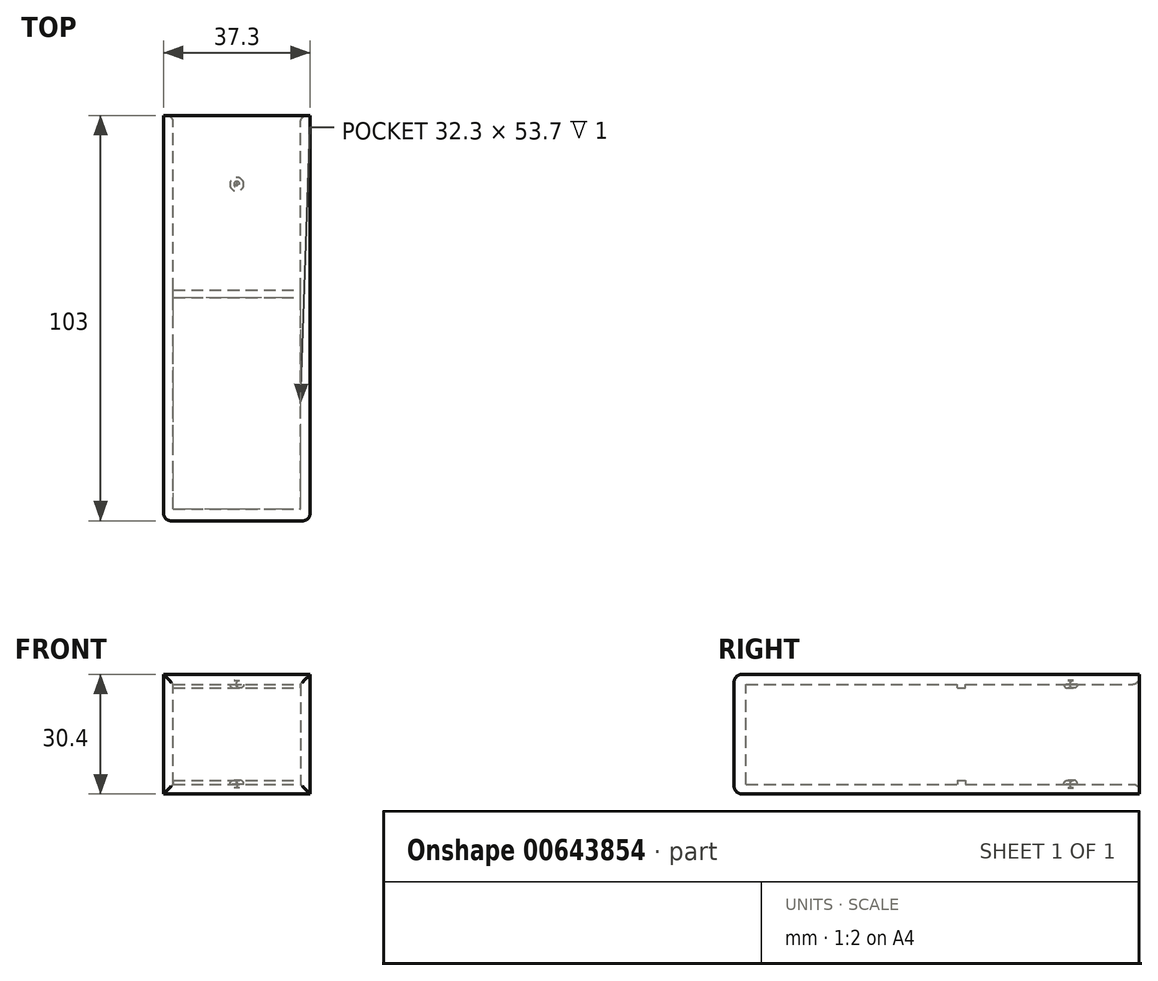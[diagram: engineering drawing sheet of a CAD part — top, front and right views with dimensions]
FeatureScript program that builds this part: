
annotation { "Feature Type Name" : "Feature", "Feature Type Description" : "" }
export const myFeature = defineFeature(function(context is Context, id is Id, definition is map)
    precondition{}
    {
        {
            var Q0;
            Q0=qCreatedBy(makeId("Front.planeOp"),FACE);
            var sketch = newSketch(context, id + "F0", { "sketchPlane" : qUnion([Q0])});
            skLineSegment(sketch, "E0.top", {"start": v(-16.49, 15.07) * mm, "end": v(15.81, 15.07) * mm});
            skLineSegment(sketch, "E0.left", {"start": v(-16.49, -10.33) * mm, "end": v(-16.49, 15.07) * mm});
            skLineSegment(sketch, "E1", {"start": v(15.81, 15.07) * mm, "end": v(15.81, -10.33) * mm});
            skLineSegment(sketch, "E2", {"start": v(-16.49, -10.33) * mm, "end": v(15.81, -10.33) * mm});
            skLineSegment(sketch, "E3.0", {"start": v(-18.99, 17.57) * mm, "end": v(18.31, 17.57) * mm});
            skLineSegment(sketch, "E3.1", {"start": v(-18.99, -12.83) * mm, "end": v(-18.99, 17.57) * mm});
            skLineSegment(sketch, "E3.2", {"start": v(-18.99, -12.83) * mm, "end": v(18.31, -12.83) * mm});
            skLineSegment(sketch, "E3.3", {"start": v(18.31, 17.57) * mm, "end": v(18.31, -12.83) * mm});
            skSolve(sketch);
        }
        {
            var Q0;
            Q0 = qSketchRegion(id + "F0", true);
            extrude(context, id + "F1", {"entities" : qUnion([Q0]), "depth" : 100 * mm, "offsetDistance" : 25 * mm});
        }
        {
            var Q0;
            Q0=makeQuery(id+"F1.opExtrude","CAP_FACE",FACE,{"disambiguationData":[OSD([sQuery(id+"F0.wireOp",EDGE,"E0.top"),sQuery(id+"F0.wireOp",EDGE,"E0.left"),sQuery(id+"F0.wireOp",EDGE,"E1"),sQuery(id+"F0.wireOp",EDGE,"E2"),sQuery(id+"F0.wireOp",EDGE,"E3.0"),sQuery(id+"F0.wireOp",EDGE,"E3.1"),sQuery(id+"F0.wireOp",EDGE,"E3.2"),sQuery(id+"F0.wireOp",EDGE,"E3.3")])],"isStart":false});
            var sketch = newSketch(context, id + "F2", { "sketchPlane" : qUnion([Q0])});
            skLineSegment(sketch, "E4.bottom", {"start": v(-18.99, 17.57) * mm, "end": v(18.31, 17.57) * mm});
            skLineSegment(sketch, "E4.top", {"start": v(-18.99, -12.83) * mm, "end": v(18.31, -12.83) * mm});
            skLineSegment(sketch, "E4.left", {"start": v(-18.99, 17.57) * mm, "end": v(-18.99, -12.83) * mm});
            skLineSegment(sketch, "E4.right", {"start": v(18.31, 17.57) * mm, "end": v(18.31, -12.83) * mm});
            skSolve(sketch);
        }
        {
            var Q0;
            Q0 = qSketchRegion(id + "F2", true);
            extrude(context, id + "F3", {"entities" : qUnion([Q0]), "operationType" : NewBodyOperationType.ADD, "depth" : 3 * mm, "offsetDistance" : 25 * mm});
        }
        {
            var Q0;
            Q0=makeQuery(id+"F3.opExtrude","CAP_FACE",FACE,{"disambiguationData":[OSD([sQuery(id+"F2.wireOp",EDGE,"E4.bottom"),sQuery(id+"F2.wireOp",EDGE,"E4.top"),sQuery(id+"F2.wireOp",EDGE,"E4.left"),sQuery(id+"F2.wireOp",EDGE,"E4.right")])],"isStart":false});
            fillet(context, id + "F4", {"entities" : qUnion([Q0]), "radius" : 2 * mm, "tangentPropagation" : true, "allowEdgeOverflow" : false});
        }
        {
            var Q0;
            Q0=makeQuery(id+"F1.opExtrude","CAP_EDGE",EDGE,{"disambiguationData":[OSD([sQuery(id+"F0.wireOp",EDGE,"E1")])],"isStart":true});
            var Q1;
            Q1=makeQuery(id+"F1.opExtrude","CAP_EDGE",EDGE,{"disambiguationData":[OSD([sQuery(id+"F0.wireOp",EDGE,"E0.top")])],"isStart":true});
            var Q2;
            Q2=makeQuery(id+"F1.opExtrude","CAP_EDGE",EDGE,{"disambiguationData":[OSD([sQuery(id+"F0.wireOp",EDGE,"E0.left")])],"isStart":true});
            var Q3;
            Q3=makeQuery(id+"F1.opExtrude","CAP_EDGE",EDGE,{"disambiguationData":[OSD([sQuery(id+"F0.wireOp",EDGE,"E2")])],"isStart":true});
            fillet(context, id + "F5", {"entities" : qUnion([Q0, Q1, Q2, Q3]), "radius" : 1.75 * mm, "tangentPropagation" : true, "allowEdgeOverflow" : false});
        }
        {
            var Q0;
            Q0=makeQuery(id+"F1.opExtrude","SWEPT_FACE",FACE,{"disambiguationData":[OSD([sQuery(id+"F0.wireOp",EDGE,"E2")])]});
            var sketch = newSketch(context, id + "F6", { "sketchPlane" : qUnion([Q0])});
            skPoint(sketch, "E5.0", {"position": v(-0.34, -1.75) * mm});
            skLineSegment(sketch, "E6", {"start": v(-0.34, -1.75) * mm, "end": v(-0.34, -20.52) * mm, "construction": true});
            skCircle(sketch, "E7", {"center": v(-0.34, -17.5) * mm, "radius": 1.75 * mm});
            skLineSegment(sketch, "E8.0", {"start": v(-18.24, 0) * mm, "end": v(17.56, 0) * mm});
            skSolve(sketch);
        }
        {
            var Q0;
            Q0 = qSketchRegion(id + "F6", true);
            extrude(context, id + "F7", {"entities" : qUnion([Q0]), "operationType" : NewBodyOperationType.REMOVE, "oppositeDirection" : true, "depth" : 1 * mm, "offsetDistance" : 25 * mm});
        }
        {
            var Q0;
            Q0=makeQuery(id+"F7.boolean.opBoolean","COPY",FACE,{"derivedFrom":makeQuery(id+"F7.opExtrude","CAP_FACE",FACE,{"disambiguationData":[OSD([sQuery(id+"F6.wireOp",EDGE,"E7")])],"isStart":false})});
            fillet(context, id + "F8", {"entities" : qUnion([Q0]), "radius" : 1 * mm, "tangentPropagation" : true, "allowEdgeOverflow" : false});
        }
        {
            var Q0;
            Q0=makeQuery(id+"F1.opExtrude","SWEPT_FACE",FACE,{"disambiguationData":[OSD([sQuery(id+"F0.wireOp",EDGE,"E0.top")])]});
            var sketch = newSketch(context, id + "F9", { "sketchPlane" : qUnion([Q0])});
            skCircle(sketch, "E9.0", {"center": v(-0.34, 17.5) * mm, "radius": 1.75 * mm});
            skSolve(sketch);
        }
        {
            var Q0;
            Q0 = qSketchRegion(id + "F9", true);
            extrude(context, id + "F10", {"entities" : qUnion([Q0]), "operationType" : NewBodyOperationType.REMOVE, "oppositeDirection" : true, "depth" : 1 * mm, "offsetDistance" : 25 * mm});
        }
        {
            var Q0;
            Q0=makeQuery(id+"F10.boolean.opBoolean","COPY",EDGE,{"derivedFrom":makeQuery(id+"F10.opExtrude","CAP_EDGE",EDGE,{"disambiguationData":[OSD([sQuery(id+"F9.wireOp",EDGE,"E9.0")])],"isStart":false})});
            fillet(context, id + "F11", {"entities" : qUnion([Q0]), "radius" : 1 * mm, "tangentPropagation" : true, "allowEdgeOverflow" : false});
        }
        {
            var Q0;
            Q0=makeQuery(id+"F1.opExtrude","SWEPT_FACE",FACE,{"disambiguationData":[OSD([sQuery(id+"F0.wireOp",EDGE,"E2")])]});
            var sketch = newSketch(context, id + "F12", { "sketchPlane" : qUnion([Q0])});
            skLineSegment(sketch, "E10", {"start": v(-16.49, -44.3) * mm, "end": v(15.81, -44.3) * mm});
            skCircle(sketch, "E11.0", {"center": v(-0.34, -17.5) * mm, "radius": 0.75 * mm, "construction": true});
            skCircle(sketch, "E12.0.0", {"center": v(-0.34, -17.5) * mm, "radius": 0.75 * mm});
            skLineSegment(sketch, "E13.0", {"start": v(-16.49, -46.3) * mm, "end": v(15.81, -46.3) * mm});
            skLineSegment(sketch, "E14.0", {"start": v(-29.33, 10.35) * mm, "end": v(-29.33, -111.35) * mm});
            skLineSegment(sketch, "E14.1", {"start": v(28.66, 10.35) * mm, "end": v(-29.33, 10.35) * mm});
            skLineSegment(sketch, "E14.2", {"start": v(28.66, -111.35) * mm, "end": v(28.66, 10.35) * mm});
            skLineSegment(sketch, "E14.3", {"start": v(-29.33, -111.35) * mm, "end": v(28.66, -111.35) * mm});
            skSolve(sketch);
        }
        {
            var Q0;
            {var subQ0=sQuery(id+"F12.wireOp",EDGE,"E10");Q0=makeQuery(id+"F12.imprint","IMPRINT",FACE,{"disambiguationData":[TD([[makeQuery(id+"F12.imprint","IMPRINT",EDGE,{"derivedFrom":subQ0}),-1.0]])]});}
            extrude(context, id + "F13", {"entities" : qUnion([Q0]), "operationType" : NewBodyOperationType.ADD, "depth" : 1 * mm, "offsetDistance" : 25 * mm});
        }
        {
            var Q0;
            Q0=makeQuery(id+"F1.opExtrude","SWEPT_FACE",FACE,{"disambiguationData":[OSD([sQuery(id+"F0.wireOp",EDGE,"E0.top")])]});
            var sketch = newSketch(context, id + "F14", { "sketchPlane" : qUnion([Q0])});
            skLineSegment(sketch, "E15.0", {"start": v(-16.49, 46.3) * mm, "end": v(15.81, 46.3) * mm});
            skLineSegment(sketch, "E16.0", {"start": v(-16.49, 44.3) * mm, "end": v(15.81, 44.3) * mm});
            skSolve(sketch);
        }
        {
            var Q0;
            {var subQ0=sQuery(id+"F14.wireOp",EDGE,"E15.0");Q0=makeQuery(id+"F14.imprint","IMPRINT",FACE,{"disambiguationData":[TD([[makeQuery(id+"F14.imprint","IMPRINT",EDGE,{"derivedFrom":subQ0}),-1.0]])]});}
            extrude(context, id + "F15", {"entities" : qUnion([Q0]), "operationType" : NewBodyOperationType.ADD, "depth" : 1 * mm, "offsetDistance" : 25 * mm});
        }
    });
